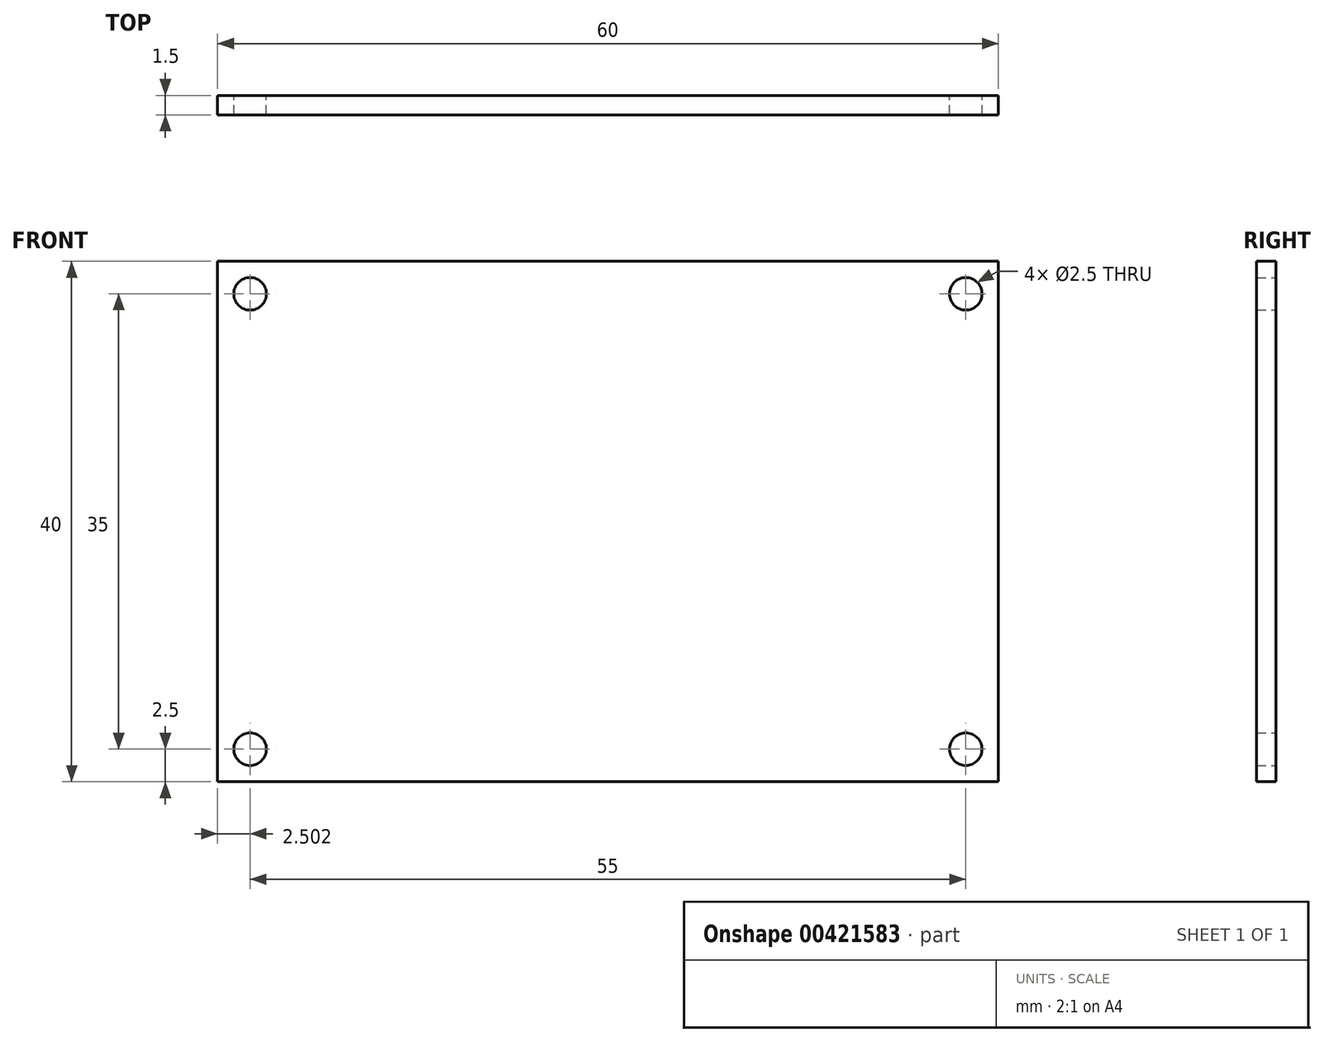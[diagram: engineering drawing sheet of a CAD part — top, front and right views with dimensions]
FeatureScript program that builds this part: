
annotation { "Feature Type Name" : "Feature", "Feature Type Description" : "" }
export const myFeature = defineFeature(function(context is Context, id is Id, definition is map)
    precondition{}
    {
        {
            var Q0;
            Q0=qCreatedBy(makeId("Front.planeOp"),FACE);
            var sketch = newSketch(context, id + "F0", { "sketchPlane" : qUnion([Q0])});
            skLineSegment(sketch, "E0.bottom", {"start": v(-49.72, 43.01) * mm, "end": v(10.28, 43.01) * mm});
            skLineSegment(sketch, "E0.top", {"start": v(-49.72, 3.01) * mm, "end": v(10.28, 3.01) * mm});
            skLineSegment(sketch, "E0.left", {"start": v(-49.72, 43.01) * mm, "end": v(-49.72, 3.01) * mm});
            skLineSegment(sketch, "E0.right", {"start": v(10.28, 43.01) * mm, "end": v(10.28, 3.01) * mm});
            skCircle(sketch, "E1", {"center": v(-47.22, 40.51) * mm, "radius": 1.25 * mm});
            skCircle(sketch, "E2.MirrorC", {"center": v(7.78, 40.51) * mm, "radius": 1.25 * mm});
            skCircle(sketch, "E3.MirrorC", {"center": v(-47.22, 5.51) * mm, "radius": 1.25 * mm});
            skCircle(sketch, "E4.MirrorC", {"center": v(7.78, 5.51) * mm, "radius": 1.25 * mm});
            skSolve(sketch);
        }
        {
            var Q0;
            Q0=makeQuery(id+"F0.imprint","IMPRINT",FACE,{"disambiguationData":[TD([[makeQuery(id+"F0.imprint","IMPRINT",EDGE,{"derivedFrom":sQuery(id+"F0.wireOp",EDGE,"E0.bottom")}),-1.0]])]});
            extrude(context, id + "F1", {"entities" : qUnion([Q0]), "depth" : 1.5 * mm, "offsetDistance" : 25 * mm});
        }
    });
